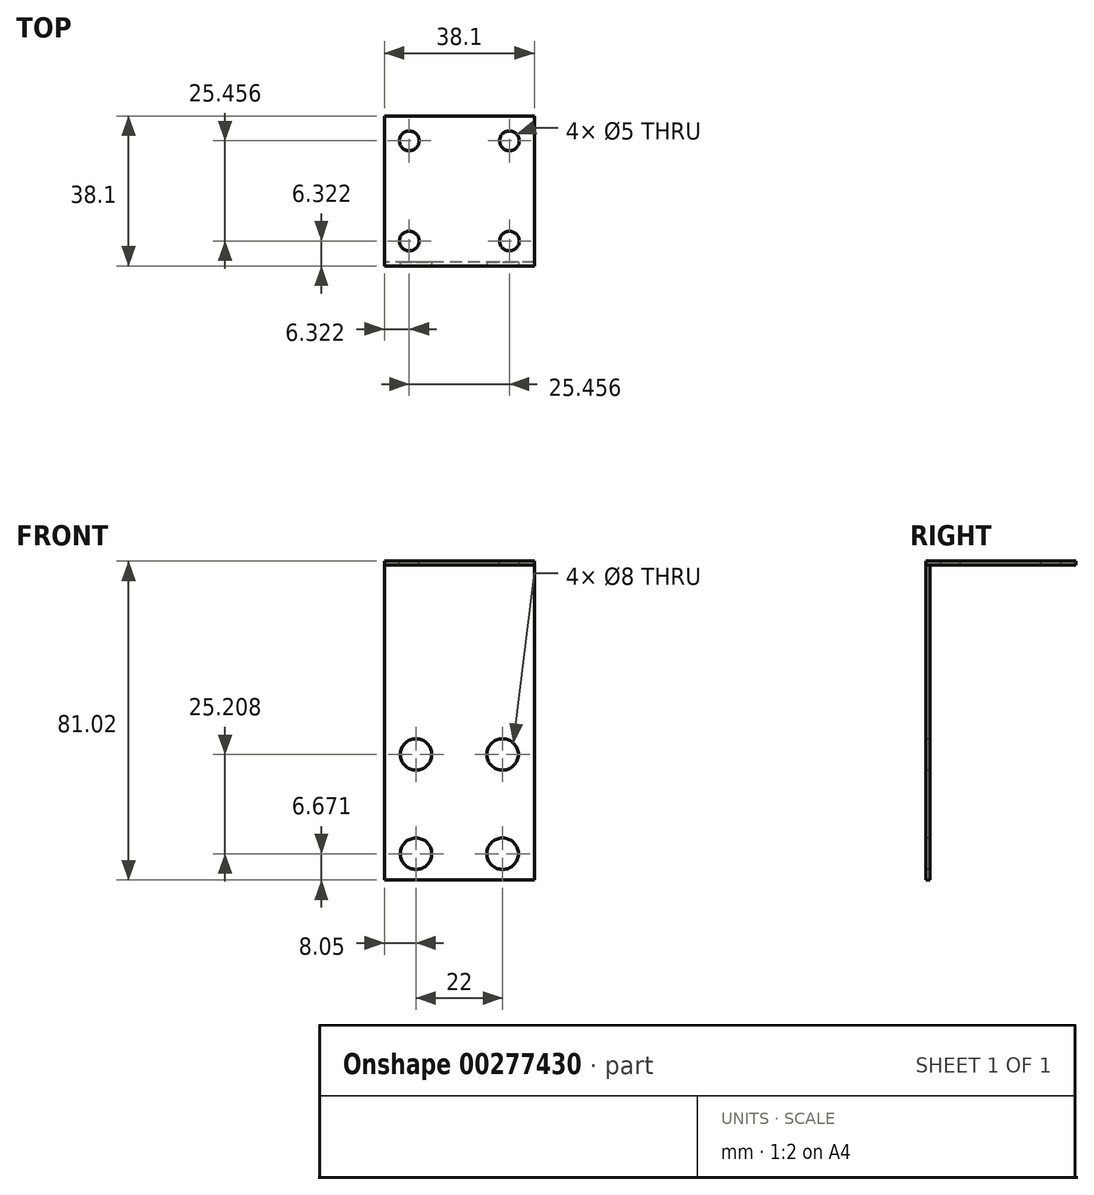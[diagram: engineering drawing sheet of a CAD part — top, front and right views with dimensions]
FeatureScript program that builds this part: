
annotation { "Feature Type Name" : "Feature", "Feature Type Description" : "" }
export const myFeature = defineFeature(function(context is Context, id is Id, definition is map)
    precondition{}
    {
        {
            var Q0;
            Q0=qCreatedBy(makeId("Top.planeOp"),FACE);
            var sketch = newSketch(context, id + "F0", { "sketchPlane" : qUnion([Q0])});
            skLineSegment(sketch, "E0.bottom", {"start": v(19.05, 19.05) * mm, "end": v(-19.05, 19.05) * mm});
            skLineSegment(sketch, "E0.top", {"start": v(19.05, -19.05) * mm, "end": v(-19.05, -19.05) * mm});
            skLineSegment(sketch, "E0.left", {"start": v(19.05, 19.05) * mm, "end": v(19.05, -19.05) * mm});
            skLineSegment(sketch, "E0.right", {"start": v(-19.05, 19.05) * mm, "end": v(-19.05, -19.05) * mm});
            skPoint(sketch, "E0.middle", {"position": v(0, 0) * mm});
            skSolve(sketch);
        }
        {
            var Q0;
            Q0=makeQuery(id+"F0.imprint","IMPRINT",FACE,{"disambiguationData":[TD([[makeQuery(id+"F0.imprint","IMPRINT",EDGE,{"derivedFrom":sQuery(id+"F0.wireOp",EDGE,"E0.bottom")}),1.0]])]});
            var Q1;
            Q1 = qSketchRegion(id + "F2", true);
            extrude(context, id + "F1", {"entities" : qUnion([Q0, Q1]), "depth" : 1.02 * mm});
        }
        {
            var Q0;
            Q0=makeQuery(id+"F1.opExtrude","CAP_FACE",FACE,{"disambiguationData":[OSD([sQuery(id+"F0.wireOp",EDGE,"E0.bottom"),sQuery(id+"F0.wireOp",EDGE,"E0.top"),sQuery(id+"F0.wireOp",EDGE,"E0.left"),sQuery(id+"F0.wireOp",EDGE,"E0.right")])],"isStart":false});
            var sketch = newSketch(context, id + "F2", { "sketchPlane" : qUnion([Q0])});
            skCircle(sketch, "E1", {"center": v(0, 0) * mm, "radius": 14.6 * mm});
            skSolve(sketch);
        }
        {
            var Q0;
            Q0=makeQuery(id+"F1.opExtrude","SWEPT_FACE",FACE,{"disambiguationData":[OSD([sQuery(id+"F0.wireOp",EDGE,"E0.top")])]});
            var sketch = newSketch(context, id + "F3", { "sketchPlane" : qUnion([Q0])});
            skLineSegment(sketch, "E2.bottom", {"start": v(-19.05, 0) * mm, "end": v(19.05, 0) * mm});
            skLineSegment(sketch, "E2.top", {"start": v(-19.05, -80) * mm, "end": v(19.05, -80) * mm});
            skLineSegment(sketch, "E2.left", {"start": v(-19.05, 0) * mm, "end": v(-19.05, -80) * mm});
            skLineSegment(sketch, "E2.right", {"start": v(19.05, 0) * mm, "end": v(19.05, -80) * mm});
            skSolve(sketch);
        }
        {
            var Q0;
            Q0 = qSketchRegion(id + "F3", true);
            extrude(context, id + "F4", {"entities" : qUnion([Q0]), "oppositeDirection" : true, "depth" : 1.02 * mm});
        }
        {
            var Q0;
            Q0=makeQuery(id+"F2.imprint","IMPRINT",FACE,{"disambiguationData":[TD([[makeQuery(id+"F2.imprint","IMPRINT",EDGE,{"derivedFrom":sQuery(id+"F2.wireOp",EDGE,"E1")}),-1.0]])]});
            var sketch = newSketch(context, id + "F5", { "sketchPlane" : qUnion([Q0])});
            skCircle(sketch, "E3", {"center": v(12.73, -12.73) * mm, "radius": 2.5 * mm});
            skCircle(sketch, "E4", {"center": v(-12.73, -12.73) * mm, "radius": 2.5 * mm});
            skCircle(sketch, "E5", {"center": v(-12.73, 12.73) * mm, "radius": 2.5 * mm});
            skCircle(sketch, "E6", {"center": v(12.73, 12.73) * mm, "radius": 2.5 * mm});
            skSolve(sketch);
        }
        {
            var Q0;
            Q0 = qSketchRegion(id + "F5", true);
            extrude(context, id + "F6", {"entities" : qUnion([Q0]), "operationType" : NewBodyOperationType.REMOVE, "oppositeDirection" : true, "depth" : 2 * mm});
        }
        {
            var Q0;
            Q0=makeQuery(id+"F3.imprint","IMPRINT",FACE,{"disambiguationData":[TD([[makeQuery(id+"F3.imprint","IMPRINT",EDGE,{"derivedFrom":sQuery(id+"F3.wireOp",EDGE,"E2.bottom")}),1.0]])]});
            var sketch = newSketch(context, id + "F7", { "sketchPlane" : qUnion([Q0])});
            skCircle(sketch, "E7", {"center": v(-11, -73.33) * mm, "radius": 4 * mm});
            skCircle(sketch, "E8", {"center": v(11, -73.33) * mm, "radius": 4 * mm});
            skLineSegment(sketch, "E9", {"start": v(-11, -73.33) * mm, "end": v(11, -73.33) * mm});
            skLineSegment(sketch, "E10", {"start": v(11, -73.33) * mm, "end": v(19.05, -73.33) * mm});
            skLineSegment(sketch, "E11", {"start": v(-11, -73.33) * mm, "end": v(-19.05, -73.33) * mm});
            skCircle(sketch, "E12", {"center": v(-11, -48.12) * mm, "radius": 4 * mm});
            skCircle(sketch, "E13", {"center": v(11, -48.12) * mm, "radius": 4 * mm});
            skLineSegment(sketch, "E14", {"start": v(-11, -73.33) * mm, "end": v(-11, -16.05) * mm});
            skLineSegment(sketch, "E15", {"start": v(11, -73.33) * mm, "end": v(11, -16.77) * mm});
            skLineSegment(sketch, "E16", {"start": v(-11, -48.12) * mm, "end": v(11, -48.12) * mm});
            skSolve(sketch);
        }
        {
            var Q0;
            {var subQ0=sQuery(id+"F7.wireOp",EDGE,"E14");var subQ1=sQuery(id+"F7.wireOp",EDGE,"E12");var subQ2=makeQuery(id+"F7.imprint","INTERSECT",VERTEX,{"derivedFrom":[subQ1,subQ0]});Q0=makeQuery(id+"F7.imprint","IMPRINT",FACE,{"disambiguationData":[TD([[makeQuery(id+"F7.imprint","IMPRINT",EDGE,{"disambiguationData":[TD([[subQ2,-1.0]])],"derivedFrom":subQ1}),1.0]])]});}
            var Q1;
            {var subQ0=sQuery(id+"F7.wireOp",EDGE,"E14");var subQ1=sQuery(id+"F7.wireOp",EDGE,"E12");var subQ2=makeQuery(id+"F7.imprint","INTERSECT",VERTEX,{"derivedFrom":[subQ1,subQ0]});Q1=makeQuery(id+"F7.imprint","IMPRINT",FACE,{"disambiguationData":[TD([[makeQuery(id+"F7.imprint","IMPRINT",EDGE,{"disambiguationData":[TD([[subQ2,1.0]])],"derivedFrom":subQ1}),1.0]])]});}
            var Q2;
            {var subQ0=sQuery(id+"F7.wireOp",EDGE,"E14");var subQ1=sQuery(id+"F7.wireOp",EDGE,"E7");var subQ2=makeQuery(id+"F7.imprint","INTERSECT",VERTEX,{"derivedFrom":[subQ1,subQ0]});Q2=makeQuery(id+"F7.imprint","IMPRINT",FACE,{"disambiguationData":[TD([[makeQuery(id+"F7.imprint","IMPRINT",EDGE,{"disambiguationData":[TD([[subQ2,1.0]])],"derivedFrom":subQ1}),1.0]])]});}
            var Q3;
            {var subQ0=sQuery(id+"F7.wireOp",EDGE,"E9");var subQ1=sQuery(id+"F7.wireOp",EDGE,"E7");var subQ2=makeQuery(id+"F7.imprint","INTERSECT",VERTEX,{"derivedFrom":[subQ1,subQ0]});Q3=makeQuery(id+"F7.imprint","IMPRINT",FACE,{"disambiguationData":[TD([[makeQuery(id+"F7.imprint","IMPRINT",EDGE,{"disambiguationData":[TD([[subQ2,1.0]])],"derivedFrom":subQ1}),1.0]])]});}
            var Q4;
            {var subQ0=sQuery(id+"F7.wireOp",EDGE,"E14");var subQ1=sQuery(id+"F7.wireOp",EDGE,"E7");var subQ2=makeQuery(id+"F7.imprint","INTERSECT",VERTEX,{"derivedFrom":[subQ1,subQ0]});Q4=makeQuery(id+"F7.imprint","IMPRINT",FACE,{"disambiguationData":[TD([[makeQuery(id+"F7.imprint","IMPRINT",EDGE,{"disambiguationData":[TD([[subQ2,-1.0]])],"derivedFrom":subQ1}),1.0]])]});}
            var Q5;
            {var subQ0=sQuery(id+"F7.wireOp",EDGE,"E15");var subQ1=sQuery(id+"F7.wireOp",EDGE,"E13");var subQ2=makeQuery(id+"F7.imprint","INTERSECT",VERTEX,{"derivedFrom":[subQ1,subQ0]});Q5=makeQuery(id+"F7.imprint","IMPRINT",FACE,{"disambiguationData":[TD([[makeQuery(id+"F7.imprint","IMPRINT",EDGE,{"disambiguationData":[TD([[subQ2,-1.0]])],"derivedFrom":subQ1}),1.0]])]});}
            var Q6;
            {var subQ0=sQuery(id+"F7.wireOp",EDGE,"E15");var subQ1=sQuery(id+"F7.wireOp",EDGE,"E13");var subQ2=makeQuery(id+"F7.imprint","INTERSECT",VERTEX,{"derivedFrom":[subQ1,subQ0]});Q6=makeQuery(id+"F7.imprint","IMPRINT",FACE,{"disambiguationData":[TD([[makeQuery(id+"F7.imprint","IMPRINT",EDGE,{"disambiguationData":[TD([[subQ2,1.0]])],"derivedFrom":subQ1}),1.0]])]});}
            var Q7;
            {var subQ0=sQuery(id+"F7.wireOp",EDGE,"E15");var subQ1=sQuery(id+"F7.wireOp",EDGE,"E8");var subQ2=makeQuery(id+"F7.imprint","INTERSECT",VERTEX,{"derivedFrom":[subQ1,subQ0]});Q7=makeQuery(id+"F7.imprint","IMPRINT",FACE,{"disambiguationData":[TD([[makeQuery(id+"F7.imprint","IMPRINT",EDGE,{"disambiguationData":[TD([[subQ2,-1.0]])],"derivedFrom":subQ1}),1.0]])]});}
            var Q8;
            {var subQ0=sQuery(id+"F7.wireOp",EDGE,"E15");var subQ1=sQuery(id+"F7.wireOp",EDGE,"E8");var subQ2=makeQuery(id+"F7.imprint","INTERSECT",VERTEX,{"derivedFrom":[subQ1,subQ0]});Q8=makeQuery(id+"F7.imprint","IMPRINT",FACE,{"disambiguationData":[TD([[makeQuery(id+"F7.imprint","IMPRINT",EDGE,{"disambiguationData":[TD([[subQ2,1.0]])],"derivedFrom":subQ1}),1.0]])]});}
            var Q9;
            {var subQ0=sQuery(id+"F7.wireOp",EDGE,"E10");var subQ1=sQuery(id+"F7.wireOp",EDGE,"E8");var subQ2=makeQuery(id+"F7.imprint","INTERSECT",VERTEX,{"derivedFrom":[subQ1,subQ0]});Q9=makeQuery(id+"F7.imprint","IMPRINT",FACE,{"disambiguationData":[TD([[makeQuery(id+"F7.imprint","IMPRINT",EDGE,{"disambiguationData":[TD([[subQ2,1.0]])],"derivedFrom":subQ1}),1.0]])]});}
            extrude(context, id + "F8", {"entities" : qUnion([Q0, Q1, Q2, Q3, Q4, Q5, Q6, Q7, Q8, Q9]), "operationType" : NewBodyOperationType.REMOVE, "oppositeDirection" : true, "depth" : 25 * mm});
        }
    });
